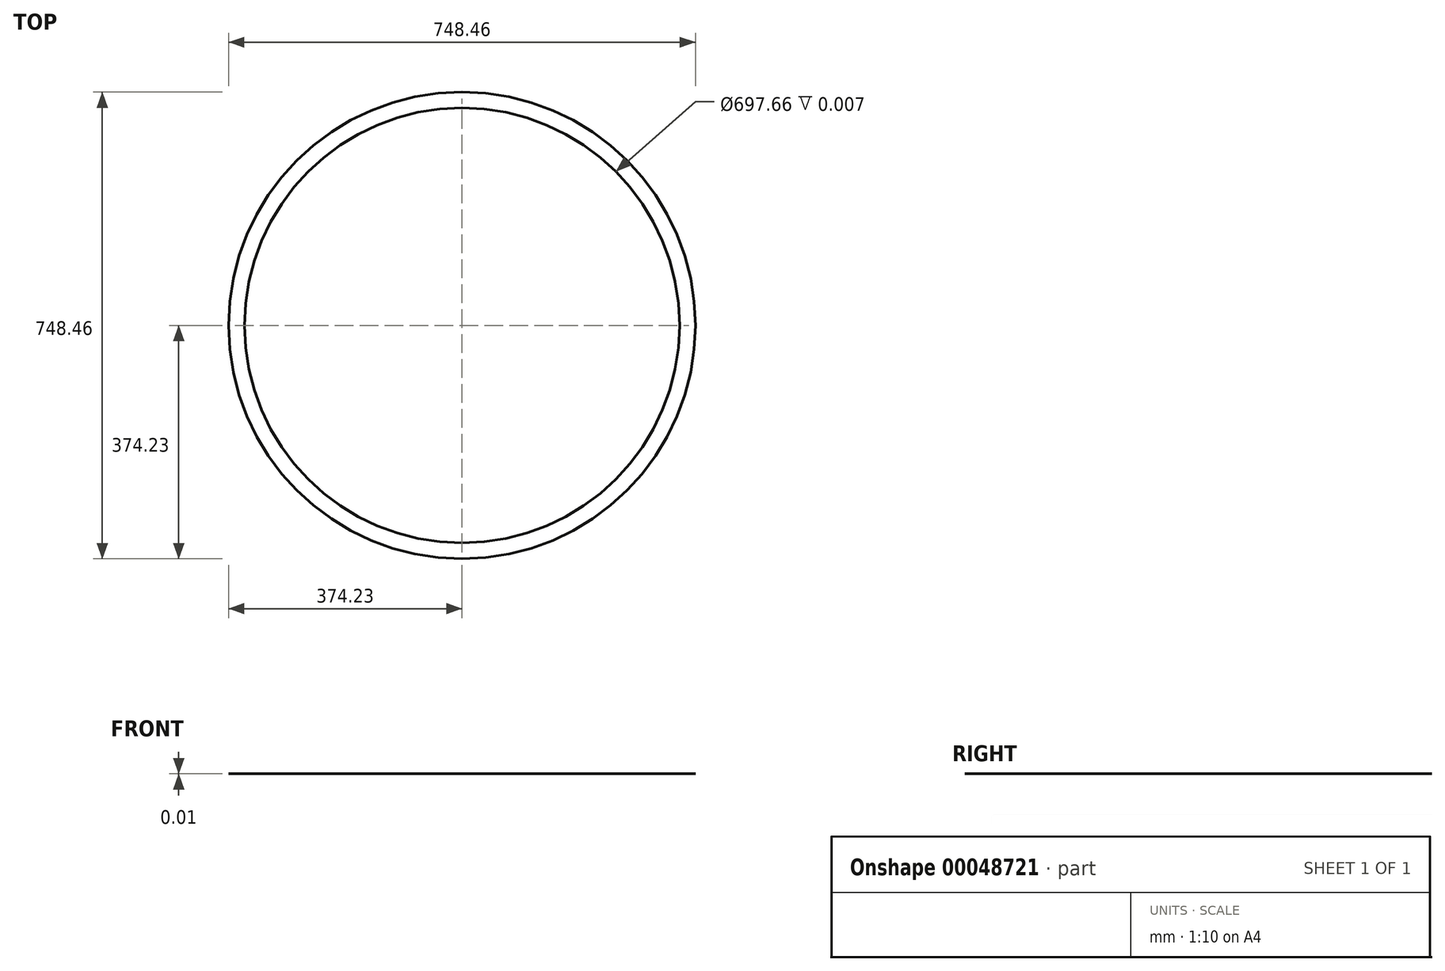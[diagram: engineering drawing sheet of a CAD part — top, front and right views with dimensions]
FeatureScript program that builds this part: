
annotation { "Feature Type Name" : "Feature", "Feature Type Description" : "" }
export const myFeature = defineFeature(function(context is Context, id is Id, definition is map)
    precondition{}
    {
        {
            var Q0;
            Q0=qCreatedBy(makeId("Top.planeOp"),FACE);
            var sketch = newSketch(context, id + "F0", { "sketchPlane" : qUnion([Q0])});
            skCircle(sketch, "E0", {"center": v(0, 0) * mm, "radius": 374.23 * mm});
            skCircle(sketch, "E1", {"center": v(0, 0) * mm, "radius": 348.83 * mm});
            skSolve(sketch);
        }
        {
            var Q0;
            Q0=makeQuery(id+"F0.imprint","IMPRINT",FACE,{"disambiguationData":[TD([[makeQuery(id+"F0.imprint","IMPRINT",EDGE,{"derivedFrom":sQuery(id+"F0.wireOp",EDGE,"E0")}),1.0]])]});
            extrude(context, id + "F1", {"entities" : qUnion([Q0]), "depth" : 3 / 406.4 * mm});
        }
    });
